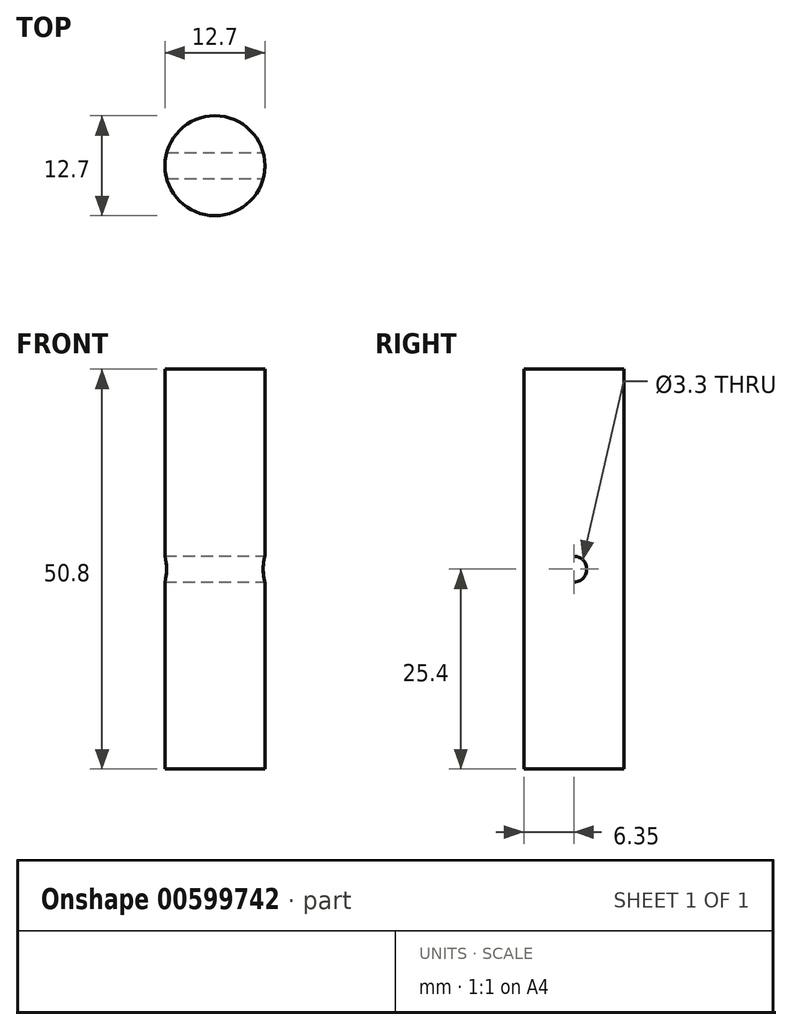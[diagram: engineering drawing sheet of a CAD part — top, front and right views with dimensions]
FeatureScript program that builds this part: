
annotation { "Feature Type Name" : "Feature", "Feature Type Description" : "" }
export const myFeature = defineFeature(function(context is Context, id is Id, definition is map)
    precondition{}
    {
        {
            var Q0;
            Q0=qCreatedBy(makeId("Top.planeOp"),FACE);
            var sketch = newSketch(context, id + "F0", { "sketchPlane" : qUnion([Q0])});
            skCircle(sketch, "E0", {"center": v(0, 0) * mm, "radius": 6.35 * mm});
            skSolve(sketch);
        }
        {
            var Q0;
            Q0=makeQuery(id+"F0.imprint","IMPRINT",FACE,{"disambiguationData":[TD([[makeQuery(id+"F0.imprint","IMPRINT",EDGE,{"derivedFrom":sQuery(id+"F0.wireOp",EDGE,"E0")}),1.0]])]});
            extrude(context, id + "F1", {"entities" : qUnion([Q0]), "depth" : 50.8 * mm, "offsetDistance" : 25.4 * mm});
        }
        {
            var Q0;
            Q0=qCreatedBy(makeId("Right.planeOp"),FACE);
            var sketch = newSketch(context, id + "F2", { "sketchPlane" : qUnion([Q0])});
            skCircle(sketch, "E1", {"center": v(0, 25.4) * mm, "radius": 1.65 * mm});
            skSolve(sketch);
        }
        {
            var Q0;
            Q0 = qSketchRegion(id + "F2", true);
            extrude(context, id + "F3", {"entities" : qUnion([Q0]), "operationType" : NewBodyOperationType.REMOVE, "endBound" : BoundingType.THROUGH_ALL, "oppositeDirection" : true, "depth" : 25.4 * mm, "offsetDistance" : 25.4 * mm});
        }
        {
            var Q0;
            Q0=makeQuery(id+"F3.boolean.opBoolean","COPY",FACE,{"derivedFrom":makeQuery(id+"F3.opExtrude","CAP_FACE",FACE,{"disambiguationData":[OSD([sQuery(id+"F2.wireOp",EDGE,"E1")])],"isStart":true})});
            extrude(context, id + "F4", {"entities" : qUnion([Q0]), "operationType" : NewBodyOperationType.REMOVE, "oppositeDirection" : true, "depth" : 25.4 * mm, "offsetDistance" : 25.4 * mm});
        }
    });
